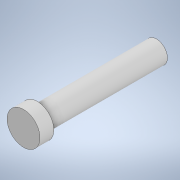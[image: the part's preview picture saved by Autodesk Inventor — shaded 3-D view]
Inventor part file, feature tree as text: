
AUTODESK INVENTOR PART (.ipt)
format: ipt  version: 2020 (Build 240168000, 168)  size: 100,352 bytes
history: native  units: mm
features: extrude x2, sketch x2
ambient origin geometry x8: Origin, YZ Plane, XZ Plane, XY Plane, X Axis, Y Axis, Z Axis, Center Point
bodies: Solid1 (feature_tree)
feature tree (4):
  extrude  "Extrusion1"  TaperAngle=0.0deg  [1 undecoded]
  extrude  "Extrusion2"  [1 undecoded]
  sketch  "Sketch1"  dims[d2=0.0mm d5=0.0mm]
  sketch  "Sketch2"
note: 2 required parameter values undecoded (feature->parameter linkage not recoverable at this tier; creation-order binding heuristic only, values carry confidence <= 0.55)
